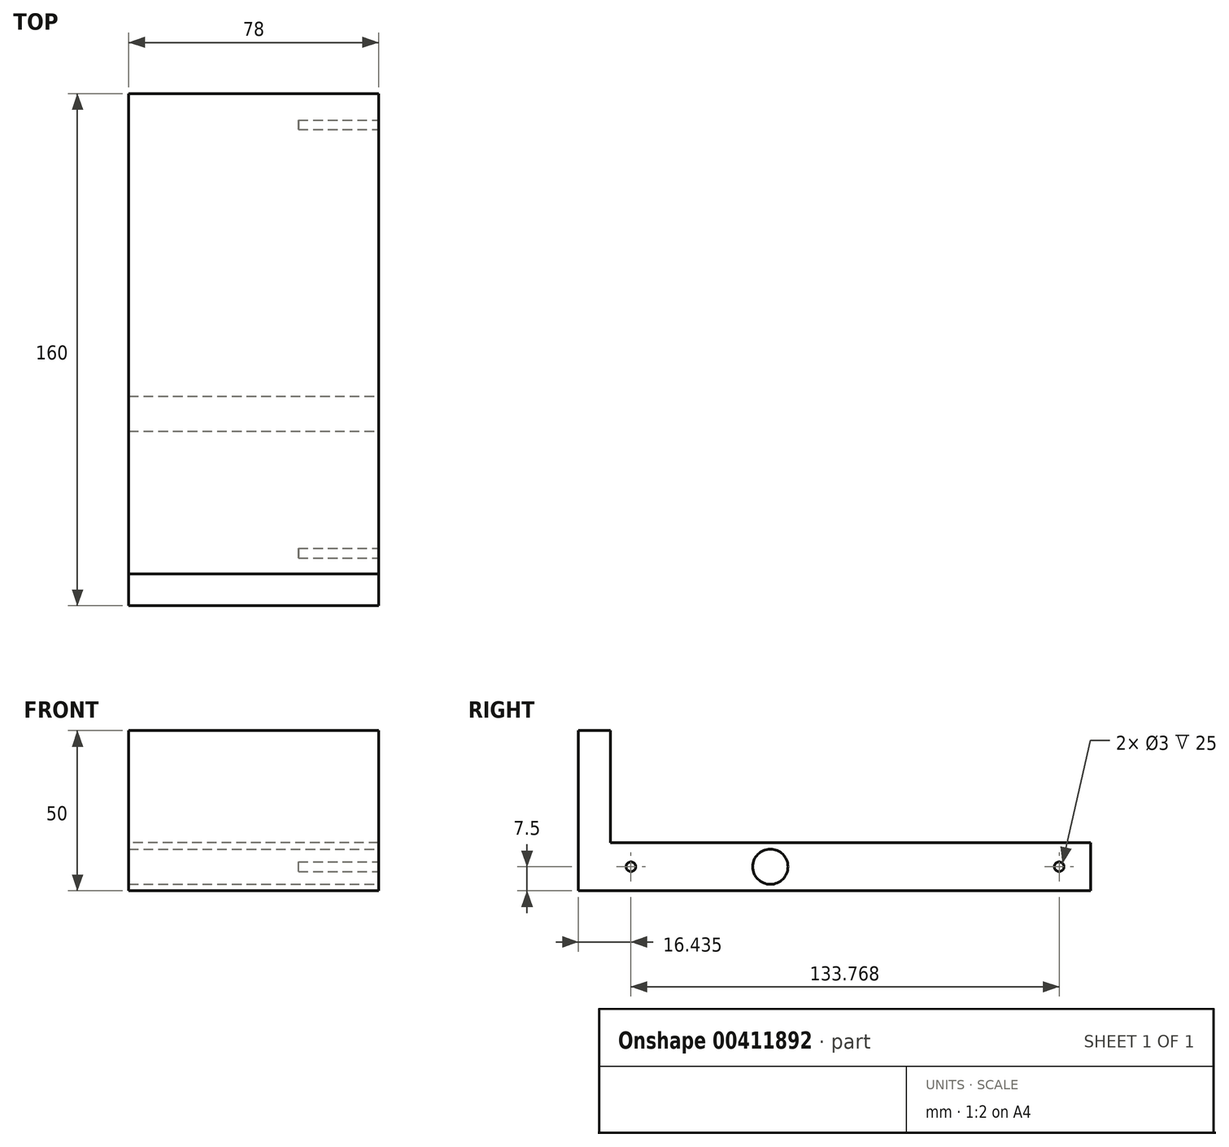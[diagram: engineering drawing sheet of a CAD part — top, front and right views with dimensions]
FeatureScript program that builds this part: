
annotation { "Feature Type Name" : "Feature", "Feature Type Description" : "" }
export const myFeature = defineFeature(function(context is Context, id is Id, definition is map)
    precondition{}
    {
        {
            var Q0;
            Q0=qCreatedBy(makeId("Right.planeOp"),FACE);
            var sketch = newSketch(context, id + "F0", { "sketchPlane" : qUnion([Q0])});
            skLineSegment(sketch, "E0", {"start": v(0, 0) * mm, "end": v(0, 50) * mm});
            skLineSegment(sketch, "E1", {"start": v(0, 50) * mm, "end": v(10, 50) * mm});
            skLineSegment(sketch, "E2", {"start": v(10, 50) * mm, "end": v(10, 15) * mm});
            skLineSegment(sketch, "E3", {"start": v(10, 15) * mm, "end": v(160, 15) * mm});
            skLineSegment(sketch, "E4", {"start": v(160, 15) * mm, "end": v(160, 0) * mm});
            skLineSegment(sketch, "E5", {"start": v(160, 0) * mm, "end": v(0, 0) * mm});
            skSolve(sketch);
        }
        {
            var Q0;
            Q0 = qSketchRegion(id + "F0", true);
            extrude(context, id + "F1", {"entities" : qUnion([Q0]), "endBound" : BoundingType.SYMMETRIC, "depth" : 78 * mm});
        }
        {
            var Q0;
            Q0=makeQuery(id+"F1.opExtrude","CAP_FACE",FACE,{"disambiguationData":[OSD([sQuery(id+"F0.wireOp",EDGE,"E0"),sQuery(id+"F0.wireOp",EDGE,"E1"),sQuery(id+"F0.wireOp",EDGE,"E2"),sQuery(id+"F0.wireOp",EDGE,"E3"),sQuery(id+"F0.wireOp",EDGE,"E4"),sQuery(id+"F0.wireOp",EDGE,"E5")])],"isStart":false});
            var sketch = newSketch(context, id + "F2", { "sketchPlane" : qUnion([Q0])});
            skCircle(sketch, "E6", {"center": v(60, 7.5) * mm, "radius": 5.5 * mm});
            skLineSegment(sketch, "E7.0.0", {"start": v(0, 0) * mm, "end": v(160, 0) * mm});
            skLineSegment(sketch, "E7.0.1", {"start": v(160, 0) * mm, "end": v(160, 15) * mm});
            skLineSegment(sketch, "E7.0.2", {"start": v(160, 15) * mm, "end": v(10, 15) * mm});
            skLineSegment(sketch, "E7.0.3", {"start": v(10, 15) * mm, "end": v(10, 50) * mm});
            skLineSegment(sketch, "E7.0.4", {"start": v(10, 50) * mm, "end": v(0, 50) * mm});
            skLineSegment(sketch, "E7.0.5", {"start": v(0, 50) * mm, "end": v(0, 0) * mm});
            skSolve(sketch);
        }
        {
            var Q0;
            Q0=makeQuery(id+"F2.imprint","IMPRINT",FACE,{"disambiguationData":[TD([[makeQuery(id+"F2.imprint","IMPRINT",EDGE,{"derivedFrom":sQuery(id+"F2.wireOp",EDGE,"E6")}),1.0]])]});
            extrude(context, id + "F3", {"entities" : qUnion([Q0]), "operationType" : NewBodyOperationType.REMOVE, "oppositeDirection" : true, "depth" : 100 * mm});
        }
        {
            var Q0;
            Q0=makeQuery(id+"F1.opExtrude","CAP_FACE",FACE,{"disambiguationData":[OSD([sQuery(id+"F0.wireOp",EDGE,"E0"),sQuery(id+"F0.wireOp",EDGE,"E1"),sQuery(id+"F0.wireOp",EDGE,"E2"),sQuery(id+"F0.wireOp",EDGE,"E3"),sQuery(id+"F0.wireOp",EDGE,"E4"),sQuery(id+"F0.wireOp",EDGE,"E5")])],"isStart":false});
            var sketch = newSketch(context, id + "F4", { "sketchPlane" : qUnion([Q0])});
            skCircle(sketch, "E8", {"center": v(150.2, 7.5) * mm, "radius": 1.5 * mm});
            skPoint(sketch, "E8.centerSnap0", {"position": v(160, 7.5) * mm});
            skCircle(sketch, "E9", {"center": v(16.43, 7.5) * mm, "radius": 1.5 * mm});
            skSolve(sketch);
        }
        {
            var Q0;
            Q0 = qSketchRegion(id + "F4", true);
            extrude(context, id + "F5", {"entities" : qUnion([Q0]), "operationType" : NewBodyOperationType.REMOVE, "oppositeDirection" : true, "depth" : 25 * mm});
        }
    });
